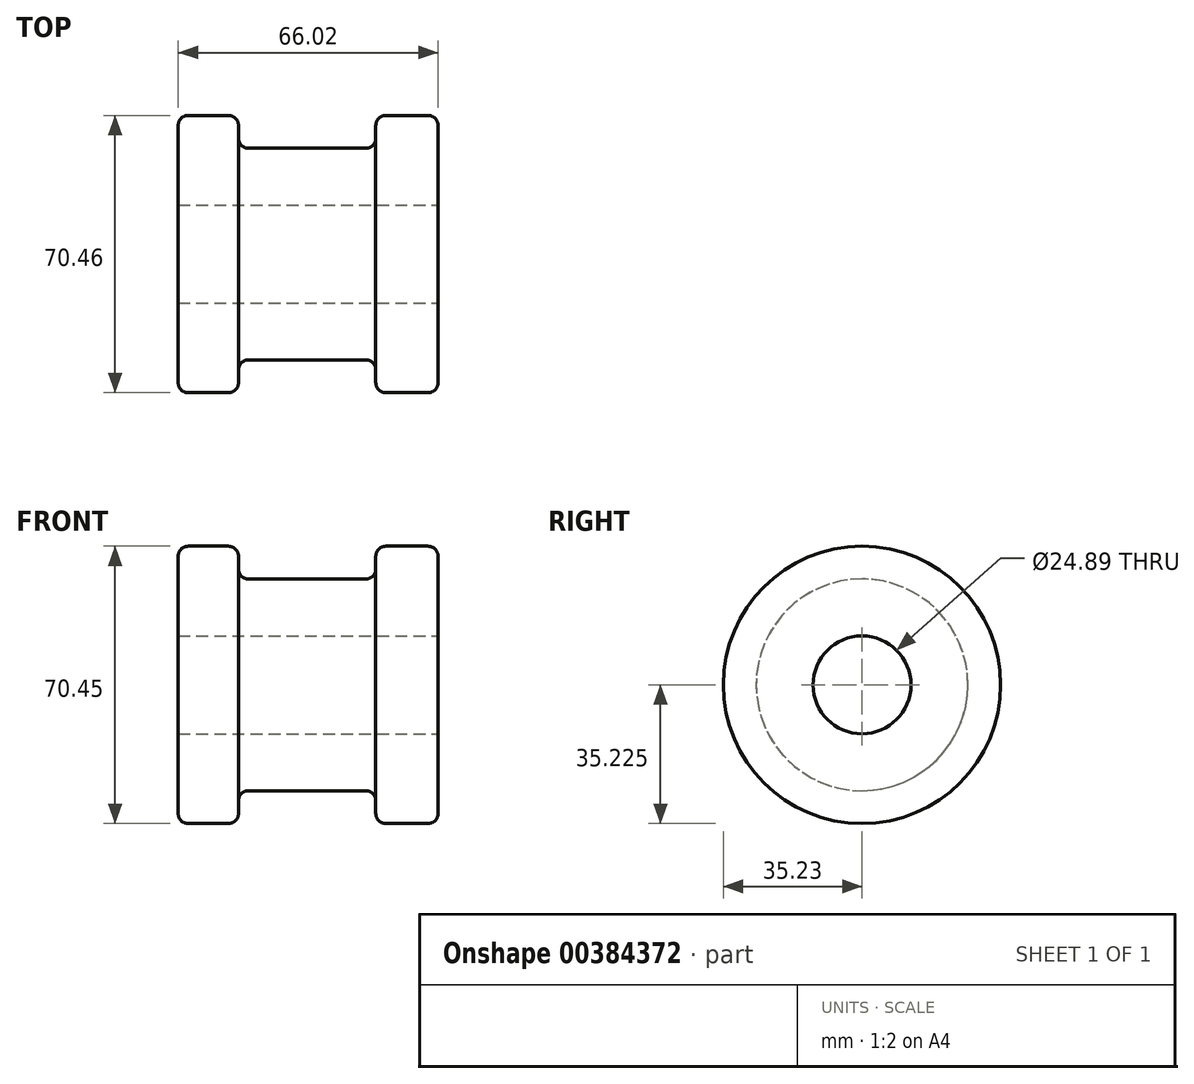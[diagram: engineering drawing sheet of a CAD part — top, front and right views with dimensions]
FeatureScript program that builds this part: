
annotation { "Feature Type Name" : "Feature", "Feature Type Description" : "" }
export const myFeature = defineFeature(function(context is Context, id is Id, definition is map)
    precondition{}
    {
        {
            var Q0;
            Q0=qCreatedBy(makeId("Front.planeOp"),FACE);
            var sketch = newSketch(context, id + "F0", { "sketchPlane" : qUnion([Q0])});
            skLineSegment(sketch, "E0", {"start": v(-54.58, 33.2) * mm, "end": v(-39.27, 33.2) * mm});
            skLineSegment(sketch, "E1", {"start": v(-39.27, 33.2) * mm, "end": v(-39.27, 24.85) * mm});
            skLineSegment(sketch, "E2", {"start": v(-39.27, 24.85) * mm, "end": v(-4.38, 24.85) * mm});
            skLineSegment(sketch, "E3", {"start": v(-4.38, 24.85) * mm, "end": v(-4.38, 33.2) * mm});
            skLineSegment(sketch, "E4", {"start": v(-4.38, 33.2) * mm, "end": v(11.44, 33.2) * mm});
            skLineSegment(sketch, "E5", {"start": v(11.44, 33.2) * mm, "end": v(11.44, -2.04) * mm});
            skLineSegment(sketch, "E6", {"start": v(11.44, -2.04) * mm, "end": v(-4.38, -2.04) * mm});
            skLineSegment(sketch, "E7", {"start": v(-4.38, -2.04) * mm, "end": v(-4.38, 6.3) * mm});
            skLineSegment(sketch, "E8", {"start": v(-4.38, 6.3) * mm, "end": v(-39.27, 6.3) * mm});
            skLineSegment(sketch, "E9", {"start": v(-39.27, 6.3) * mm, "end": v(-39.27, -2.04) * mm});
            skLineSegment(sketch, "E10", {"start": v(-39.27, -2.04) * mm, "end": v(-54.58, -2.04) * mm});
            skLineSegment(sketch, "E11", {"start": v(-54.58, -2.04) * mm, "end": v(-54.58, 33.2) * mm});
            skSolve(sketch);
        }
        {
            var Q0;
            Q0 = qSketchRegion(id + "F0", true);
            var Q1;
            Q1=sQuery(id+"F0.wireOp",EDGE,"E10");
            revolve(context, id + "F1", {"entities" : qUnion([Q0]), "axis" : qUnion([Q1]), "revolveType" : RevolveType.FULL});
        }
        {
            var Q0;
            Q0=makeQuery(id+"F1.opRevolve","SWEPT_EDGE",EDGE,{"disambiguationData":[OSD([sQuery(id+"F0.wireOp",EDGE,"E4"),sQuery(id+"F0.wireOp",EDGE,"E5")])]});
            var Q1;
            Q1=makeQuery(id+"F1.opRevolve","SWEPT_EDGE",EDGE,{"disambiguationData":[OSD([sQuery(id+"F0.wireOp",EDGE,"E0"),sQuery(id+"F0.wireOp",EDGE,"E11")])]});
            var Q2;
            Q2=makeQuery(id+"F1.opRevolve","SWEPT_EDGE",EDGE,{"disambiguationData":[OSD([sQuery(id+"F0.wireOp",EDGE,"E0"),sQuery(id+"F0.wireOp",EDGE,"E1")])]});
            var Q3;
            Q3=makeQuery(id+"F1.opRevolve","SWEPT_EDGE",EDGE,{"disambiguationData":[OSD([sQuery(id+"F0.wireOp",EDGE,"E3"),sQuery(id+"F0.wireOp",EDGE,"E4")])]});
            var Q4;
            Q4=makeQuery(id+"F1.opRevolve","SWEPT_EDGE",EDGE,{"disambiguationData":[OSD([sQuery(id+"F0.wireOp",EDGE,"E2"),sQuery(id+"F0.wireOp",EDGE,"E3")])]});
            var Q5;
            Q5=makeQuery(id+"F1.opRevolve","SWEPT_EDGE",EDGE,{"disambiguationData":[OSD([sQuery(id+"F0.wireOp",EDGE,"E1"),sQuery(id+"F0.wireOp",EDGE,"E2")])]});
            fillet(context, id + "F2", {"entities" : qUnion([Q0, Q1, Q2, Q3, Q4, Q5]), "radius" : 2.54 * mm, "tangentPropagation" : true, "allowEdgeOverflow" : false});
        }
        {
            var Q0;
            Q0=makeQuery(id+"F1.opRevolve","SWEPT_FACE",FACE,{"disambiguationData":[OSD([sQuery(id+"F0.wireOp",EDGE,"E5")])]});
            var sketch = newSketch(context, id + "F3", { "sketchPlane" : qUnion([Q0])});
            skCircle(sketch, "E12", {"center": v(0, -2.04) * mm, "radius": 22.47 * mm});
            skSolve(sketch);
        }
        {
            var Q0;
            Q0=sQuery(id+"F3.wireOp",VERTEX,"E12.center");
            var Q1;
            Q1=makeQuery(id+"F1.opRevolve","SWEPT_BODY",BODY,{"disambiguationData":[OSD([sQuery(id+"F0.wireOp",EDGE,"E0"),sQuery(id+"F0.wireOp",EDGE,"E1"),sQuery(id+"F0.wireOp",EDGE,"E2"),sQuery(id+"F0.wireOp",EDGE,"E3"),sQuery(id+"F0.wireOp",EDGE,"E4"),sQuery(id+"F0.wireOp",EDGE,"E5"),sQuery(id+"F0.wireOp",EDGE,"E6"),sQuery(id+"F0.wireOp",EDGE,"E7"),sQuery(id+"F0.wireOp",EDGE,"E8"),sQuery(id+"F0.wireOp",EDGE,"E9"),sQuery(id+"F0.wireOp",EDGE,"E10"),sQuery(id+"F0.wireOp",EDGE,"E11")])]});
            hole(context, id + "F4", {"style" : HoleStyle.SIMPLE, "endStyle" : HoleEndStyle.BLIND, "holeDiameter" : 24.9 * mm, "holeDepth" : 101.6 * mm, "isTappedThrough" : true, "tappedDepth" : 12.7 * mm, "tapClearance" : 3, "locations" : qUnion([Q0]), "scope" : qUnion([Q1])});
        }
    });
